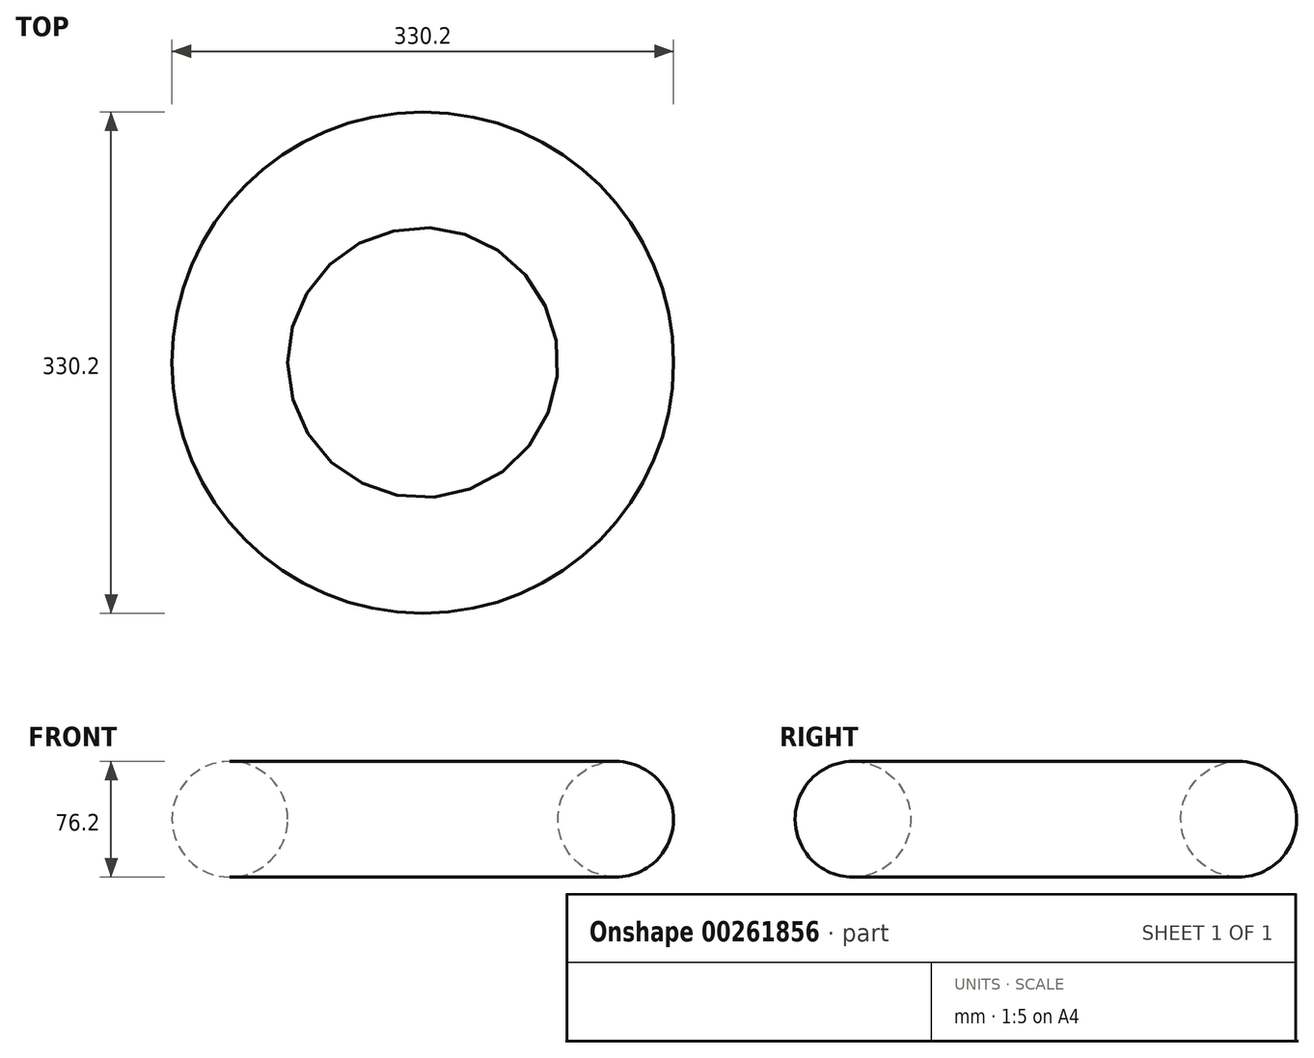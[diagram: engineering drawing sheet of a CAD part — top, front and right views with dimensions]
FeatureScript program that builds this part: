
annotation { "Feature Type Name" : "Feature", "Feature Type Description" : "" }
export const myFeature = defineFeature(function(context is Context, id is Id, definition is map)
    precondition{}
    {
        {
            var Q0;
            Q0=qCreatedBy(makeId("Front.planeOp"),FACE);
            var sketch = newSketch(context, id + "F0", { "sketchPlane" : qUnion([Q0])});
            skCircle(sketch, "E0", {"center": v(-127, 25.18) * mm, "radius": 38.1 * mm});
            skLineSegment(sketch, "E1", {"start": v(0, -77.97) * mm, "end": v(0, 77.39) * mm, "construction": true});
            skSolve(sketch);
        }
        {
            var Q0;
            Q0=makeQuery(id+"F0.imprint","IMPRINT",FACE,{"disambiguationData":[TD([[makeQuery(id+"F0.imprint","IMPRINT",EDGE,{"derivedFrom":sQuery(id+"F0.wireOp",EDGE,"E0")}),1.0]])]});
            var Q1;
            Q1=sQuery(id+"F0.wireOp",EDGE,"E1");
            revolve(context, id + "F1", {"entities" : qUnion([Q0]), "axis" : qUnion([Q1]), "revolveType" : RevolveType.FULL});
        }
    });
